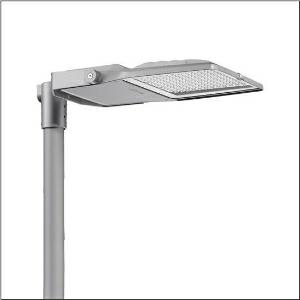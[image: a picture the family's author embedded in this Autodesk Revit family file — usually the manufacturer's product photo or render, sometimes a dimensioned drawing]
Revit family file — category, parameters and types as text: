
# Revit family: floodlight_fl_21_iq_midi___pl52_5xa7781f2d3a_fab9
name_source: partatom
category: Lighting Fixtures
units: mm (PartAtom-declared; Revit-internal decimal feet)

## family parameters
Cut with Voids When Loaded = No
Host = Face
Light Source = No
Part Type = Normal
Room Calculation Point = No
Round Connector Dimension = Use Diameter
Shared = No

## types (1)
- --- (1 x LED, 35760 lm, 270.2 W, 3000K)
    Apparent Load = 270 VA
    CIE Flux Codes = 26 60 98 100 100
    Color Rendering = 70
    Color Temperature = 3000K
    Default Elevation = 1800 mm
    Description = Floodlight FL 21 iQ midi, floodlight, primary light control with lens, of PMMA, primary optical cover: protective disc, of toughened safety glass, transparent, light distribution: PL52, light emission: direct distribution, installation type: surface-mounted, lamps: LED, High Power LED, rated values: 35.760lm | 270,2W | 132,3lm/W (begin service life); end service life: 35.760lm | 286,6W; at 50% lumin. flux: 17.880lm | 117,4W | 152,3lm/W, colour temperature: 3000K, colour rendering: CRI > 70, light colour: 730, light setting 1 begin service life: 100% | 35.760lm | 270,2W | 132,3lm/W | 3.000K, light setting 1 end service life: 286,6W, further light settings possible, control: optimised constant luminous flux control (CLO 2.0), Desk-Remote (wireless, voltage-free reading and setting of iQ features in the workshop via application-optimized NFC function/RFID function), Light-Fading, Smart-Wire, Night-Set, Lumen-Switch, Temp-Guard, Auto-Match, pre-setting: linear dimming characteristic, with terminal, 6-pole, mains connection: 220..240V, AC, 50/60Hz, luminaire housing, of diecast aluminium, powder-coated, SITECO metallic grey (DB 702S), corrosivity category C5 mid according to DIN EN ISO 12944suitable for swimming poolschlorine-resistant, sealing non-destructively replaceable, please order mast flange separately, mast bracket, of steel, galvanised, powder-coated, SITECO metallic grey (DB 702S), protection rating (complete): IP66, insulation class (complete): insulation class II (safety insulation), certification: CE, ENEC, VDE, protection symbol: D, impact resistance: IK08, permissible operating ambient temperature: -40..+40°C, permissible operating ambient temperature for outdoor applications: -40..+50°C, standard: DIN EN 12944, LABS conformity tested according to VDMA 24364:2018-05, packaging unit: 1 piece

Light Distribution: PL52
    Height = 76 mm
    Lamp = 1 x LED
    Lamp Light Flux = 35760 lm
    Lamp Power = 270.2 W
    Lamp count = 1
    Length = 657 mm
    Luminous efficacy = 132 lm/W
    Manufacturer = Siteco
    ModVariant = No
    Model = 5XA7781F2D3A
    Number of Poles = 1
    OnlyDefault = Yes
    Power Factor = 1
    Product Name = Floodlight FL 21 iQ midi | PL52
    Product group = floodlight | pylon annexe
    ProductGroupID = 6201
    Protection Class = Protection class II
    Protection Degree = IP 66
    RLX_Detail_Level = 1
    RLX_Emergency_Light_Flux = 0 lm
    RLX_Emergency_Type = 0
    RLX_Emergency_Type_DB = No
    RlxData = <blob elided: 153741 chars, md5=33476969>
    Socket = socket
    Standby Power = 0 W
    System Light Flux = 35760 lm
    System Power = 270 W
    Type Comments = factory setting: luminous flux: 100 % | dim-lin: 254 | 620 mA
    Type Image = l_1007123.jpg
    URL = http://relux.com
    VarID = @adj_105771
    Voltage = 0 V
    Weight = 0.00 kg
    Width = 442 mm

## geometry (parser evidence)
native form markers: Blend x4, Sweep x14
no freeform markers — native parametric forms only
